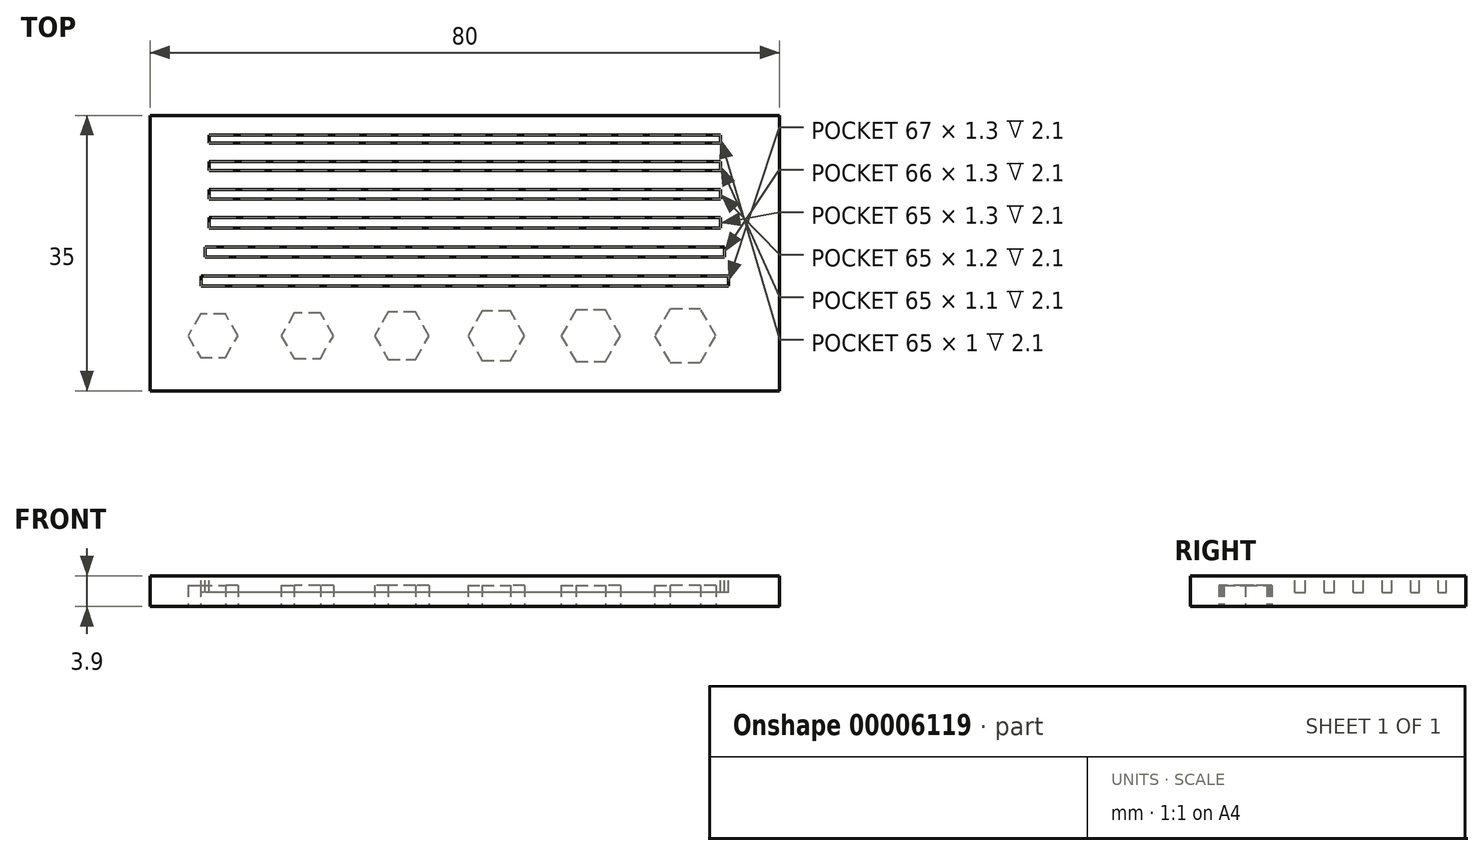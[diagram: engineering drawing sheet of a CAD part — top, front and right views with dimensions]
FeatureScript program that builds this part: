
annotation { "Feature Type Name" : "Feature", "Feature Type Description" : "" }
export const myFeature = defineFeature(function(context is Context, id is Id, definition is map)
    precondition{}
    {
        {
            var Q0;
            Q0=qCreatedBy(makeId("Top.planeOp"),FACE);
            var sketch = newSketch(context, id + "F0", { "sketchPlane" : qUnion([Q0])});
            skLineSegment(sketch, "E0.rect.bottom", {"start": v(40, -17.5) * mm, "end": v(-40, -17.5) * mm});
            skLineSegment(sketch, "E0.rect.top", {"start": v(40, 17.5) * mm, "end": v(-40, 17.5) * mm});
            skLineSegment(sketch, "E0.rect.left", {"start": v(40, -17.5) * mm, "end": v(40, 17.5) * mm});
            skLineSegment(sketch, "E0.rect.right", {"start": v(-40, -17.5) * mm, "end": v(-40, 17.5) * mm});
            skPoint(sketch, "E0.rect.middle", {"position": v(0, 0) * mm});
            skSolve(sketch);
        }
        {
            var Q0;
            Q0 = qSketchRegion(id + "F0", true);
            extrude(context, id + "F1", {"entities" : qUnion([Q0]), "depth" : 3.9 * mm});
        }
        {
            var Q0;
            Q0=makeQuery(id+"F1.opExtrude","CAP_FACE",FACE,{"disambiguationData":[OSD([sQuery(id+"F0.wireOp",EDGE,"E0.rect.bottom"),sQuery(id+"F0.wireOp",EDGE,"E0.rect.top"),sQuery(id+"F0.wireOp",EDGE,"E0.rect.left"),sQuery(id+"F0.wireOp",EDGE,"E0.rect.right")])],"isStart":false});
            var sketch = newSketch(context, id + "F2", { "sketchPlane" : qUnion([Q0])});
            skLineSegment(sketch, "E1.rect.bottom", {"start": v(32.5, 14) * mm, "end": v(-32.5, 14) * mm});
            skLineSegment(sketch, "E1.rect.top", {"start": v(32.5, 15) * mm, "end": v(-32.5, 15) * mm});
            skLineSegment(sketch, "E1.rect.left", {"start": v(32.5, 14) * mm, "end": v(32.5, 15) * mm});
            skLineSegment(sketch, "E1.rect.right", {"start": v(-32.5, 14) * mm, "end": v(-32.5, 15) * mm});
            skPoint(sketch, "E1.rect.middle", {"position": v(0, 14.5) * mm});
            skPoint(sketch, "E2.rect.middle", {"position": v(0, 11.05) * mm});
            skLineSegment(sketch, "E2.rect.bottom", {"start": v(32.5, 10.5) * mm, "end": v(-32.5, 10.5) * mm});
            skLineSegment(sketch, "E2.rect.top", {"start": v(32.5, 11.6) * mm, "end": v(-32.5, 11.6) * mm});
            skLineSegment(sketch, "E2.rect.left", {"start": v(32.5, 10.5) * mm, "end": v(32.5, 11.6) * mm});
            skLineSegment(sketch, "E2.rect.right", {"start": v(-32.5, 10.5) * mm, "end": v(-32.5, 11.6) * mm});
            skLineSegment(sketch, "E3.rect.bottom", {"start": v(32.5, 6.9) * mm, "end": v(-32.5, 6.9) * mm});
            skPoint(sketch, "E3.rect.middle", {"position": v(0, 7.5) * mm});
            skLineSegment(sketch, "E3.rect.top", {"start": v(32.5, 8.1) * mm, "end": v(-32.5, 8.1) * mm});
            skLineSegment(sketch, "E3.rect.left", {"start": v(32.5, 6.9) * mm, "end": v(32.5, 8.1) * mm});
            skLineSegment(sketch, "E3.rect.right", {"start": v(-32.5, 6.9) * mm, "end": v(-32.5, 8.1) * mm});
            skLineSegment(sketch, "E4.rect.bottom", {"start": v(32.5, 3.2) * mm, "end": v(-32.5, 3.2) * mm});
            skLineSegment(sketch, "E4.rect.top", {"start": v(32.5, 4.5) * mm, "end": v(-32.5, 4.5) * mm});
            skPoint(sketch, "E4.rect.middle", {"position": v(0, 3.85) * mm});
            skLineSegment(sketch, "E4.rect.left", {"start": v(32.5, 3.2) * mm, "end": v(32.5, 4.5) * mm});
            skLineSegment(sketch, "E4.rect.right", {"start": v(-32.5, 3.2) * mm, "end": v(-32.5, 4.5) * mm});
            skLineSegment(sketch, "E5.rect.bottom", {"start": v(33, -0.5) * mm, "end": v(-33, -0.5) * mm});
            skLineSegment(sketch, "E5.rect.top", {"start": v(33, 0.8) * mm, "end": v(-33, 0.8) * mm});
            skLineSegment(sketch, "E5.rect.left", {"start": v(33, -0.5) * mm, "end": v(33, 0.8) * mm});
            skLineSegment(sketch, "E5.rect.right", {"start": v(-33, -0.5) * mm, "end": v(-33, 0.8) * mm});
            skPoint(sketch, "E5.rect.middle", {"position": v(0, 0.15) * mm});
            skLineSegment(sketch, "E6.rect.bottom", {"start": v(33.5, -4.2) * mm, "end": v(-33.5, -4.2) * mm});
            skLineSegment(sketch, "E6.rect.top", {"start": v(33.5, -2.9) * mm, "end": v(-33.5, -2.9) * mm});
            skLineSegment(sketch, "E6.rect.left", {"start": v(33.5, -4.2) * mm, "end": v(33.5, -2.9) * mm});
            skLineSegment(sketch, "E6.rect.right", {"start": v(-33.5, -4.2) * mm, "end": v(-33.5, -2.9) * mm});
            skPoint(sketch, "E6.rect.middle", {"position": v(0, -3.55) * mm});
            skSolve(sketch);
        }
        {
            var Q0;
            Q0 = qSketchRegion(id + "F2", true);
            extrude(context, id + "F3", {"entities" : qUnion([Q0]), "operationType" : NewBodyOperationType.REMOVE, "oppositeDirection" : true, "depth" : 2.1 * mm});
        }
        {
            var Q0;
            Q0=makeQuery(id+"F1.opExtrude","CAP_FACE",FACE,{"disambiguationData":[OSD([sQuery(id+"F0.wireOp",EDGE,"E0.rect.bottom"),sQuery(id+"F0.wireOp",EDGE,"E0.rect.top"),sQuery(id+"F0.wireOp",EDGE,"E0.rect.left"),sQuery(id+"F0.wireOp",EDGE,"E0.rect.right")])],"isStart":true});
            var sketch = newSketch(context, id + "F4", { "sketchPlane" : qUnion([Q0])});
            skCircle(sketch, "E7.cCircle", {"center": v(-32, 10.5) * mm, "radius": 2.75 * mm, "construction": true});
            skLineSegment(sketch, "E7.0", {"start": v(-28.82, 10.5) * mm, "end": v(-30.41, 7.75) * mm});
            skLineSegment(sketch, "E7.1", {"start": v(-30.41, 7.75) * mm, "end": v(-33.59, 7.75) * mm});
            skLineSegment(sketch, "E7.2", {"start": v(-33.59, 7.75) * mm, "end": v(-35.18, 10.5) * mm});
            skLineSegment(sketch, "E7.3", {"start": v(-35.18, 10.5) * mm, "end": v(-33.59, 13.25) * mm});
            skLineSegment(sketch, "E7.4", {"start": v(-33.59, 13.25) * mm, "end": v(-30.41, 13.25) * mm});
            skLineSegment(sketch, "E7.5", {"start": v(-30.41, 13.25) * mm, "end": v(-28.82, 10.5) * mm});
            skPoint(sketch, "E7.0.midPoint", {"position": v(-29.62, 9.13) * mm});
            skLineSegment(sketch, "E8.1", {"start": v(-18.34, 7.63) * mm, "end": v(-21.66, 7.63) * mm});
            skLineSegment(sketch, "E8.5", {"start": v(-18.34, 13.38) * mm, "end": v(-16.68, 10.5) * mm});
            skLineSegment(sketch, "E8.2", {"start": v(-21.66, 7.63) * mm, "end": v(-23.32, 10.5) * mm});
            skLineSegment(sketch, "E8.4", {"start": v(-21.66, 13.38) * mm, "end": v(-18.34, 13.38) * mm});
            skLineSegment(sketch, "E8.3", {"start": v(-23.32, 10.5) * mm, "end": v(-21.66, 13.38) * mm});
            skPoint(sketch, "E8.0.midPoint", {"position": v(-17.51, 9.06) * mm});
            skLineSegment(sketch, "E8.0", {"start": v(-16.68, 10.5) * mm, "end": v(-18.34, 7.63) * mm});
            skCircle(sketch, "E8.cCircle", {"center": v(-20, 10.5) * mm, "radius": 2.87 * mm, "construction": true});
            skCircle(sketch, "E9.cCircle", {"center": v(-8, 10.5) * mm, "radius": 3 * mm, "construction": true});
            skLineSegment(sketch, "E9.1", {"start": v(-6.27, 7.5) * mm, "end": v(-9.73, 7.5) * mm});
            skPoint(sketch, "E9.0.midPoint", {"position": v(-5.4, 9) * mm});
            skLineSegment(sketch, "E9.3", {"start": v(-11.46, 10.5) * mm, "end": v(-9.73, 13.5) * mm});
            skLineSegment(sketch, "E9.4", {"start": v(-9.73, 13.5) * mm, "end": v(-6.27, 13.5) * mm});
            skLineSegment(sketch, "E9.2", {"start": v(-9.73, 7.5) * mm, "end": v(-11.46, 10.5) * mm});
            skLineSegment(sketch, "E9.5", {"start": v(-6.27, 13.5) * mm, "end": v(-4.54, 10.5) * mm});
            skLineSegment(sketch, "E9.0", {"start": v(-4.54, 10.5) * mm, "end": v(-6.27, 7.5) * mm});
            skLineSegment(sketch, "E10.5", {"start": v(17.88, 13.75) * mm, "end": v(19.75, 10.5) * mm});
            skLineSegment(sketch, "E11.4", {"start": v(26.05, 13.88) * mm, "end": v(29.95, 13.88) * mm});
            skLineSegment(sketch, "E12.3", {"start": v(0.4, 10.5) * mm, "end": v(2.2, 13.63) * mm});
            skCircle(sketch, "E11.cCircle", {"center": v(28, 10.5) * mm, "radius": 3.37 * mm, "construction": true});
            skLineSegment(sketch, "E12.2", {"start": v(2.2, 7.38) * mm, "end": v(0.4, 10.5) * mm});
            skLineSegment(sketch, "E12.5", {"start": v(5.8, 13.63) * mm, "end": v(7.6, 10.5) * mm});
            skLineSegment(sketch, "E11.3", {"start": v(24.1, 10.5) * mm, "end": v(26.05, 13.88) * mm});
            skCircle(sketch, "E12.cCircle", {"center": v(4, 10.5) * mm, "radius": 3.12 * mm, "construction": true});
            skCircle(sketch, "E10.cCircle", {"center": v(16, 10.5) * mm, "radius": 3.25 * mm, "construction": true});
            skPoint(sketch, "E10.0.midPoint", {"position": v(18.81, 8.88) * mm});
            skLineSegment(sketch, "E12.4", {"start": v(2.2, 13.63) * mm, "end": v(5.8, 13.63) * mm});
            skLineSegment(sketch, "E11.5", {"start": v(29.95, 13.88) * mm, "end": v(31.9, 10.5) * mm});
            skPoint(sketch, "E12.0.midPoint", {"position": v(6.7, 8.94) * mm});
            skLineSegment(sketch, "E11.1", {"start": v(29.95, 7.13) * mm, "end": v(26.05, 7.13) * mm});
            skLineSegment(sketch, "E12.1", {"start": v(5.8, 7.38) * mm, "end": v(2.2, 7.38) * mm});
            skLineSegment(sketch, "E10.2", {"start": v(14.12, 7.25) * mm, "end": v(12.25, 10.5) * mm});
            skLineSegment(sketch, "E10.4", {"start": v(14.12, 13.75) * mm, "end": v(17.88, 13.75) * mm});
            skLineSegment(sketch, "E10.3", {"start": v(12.25, 10.5) * mm, "end": v(14.12, 13.75) * mm});
            skPoint(sketch, "E11.0.midPoint", {"position": v(30.92, 8.81) * mm});
            skLineSegment(sketch, "E11.2", {"start": v(26.05, 7.13) * mm, "end": v(24.1, 10.5) * mm});
            skLineSegment(sketch, "E10.1", {"start": v(17.88, 7.25) * mm, "end": v(14.12, 7.25) * mm});
            skLineSegment(sketch, "E11.0", {"start": v(31.9, 10.5) * mm, "end": v(29.95, 7.13) * mm});
            skLineSegment(sketch, "E10.0", {"start": v(19.75, 10.5) * mm, "end": v(17.88, 7.25) * mm});
            skLineSegment(sketch, "E12.0", {"start": v(7.6, 10.5) * mm, "end": v(5.8, 7.38) * mm});
            skSolve(sketch);
        }
        {
            var Q0;
            Q0 = qSketchRegion(id + "F4", true);
            extrude(context, id + "F5", {"entities" : qUnion([Q0]), "operationType" : NewBodyOperationType.REMOVE, "oppositeDirection" : true, "depth" : 2.7 * mm});
        }
    });
